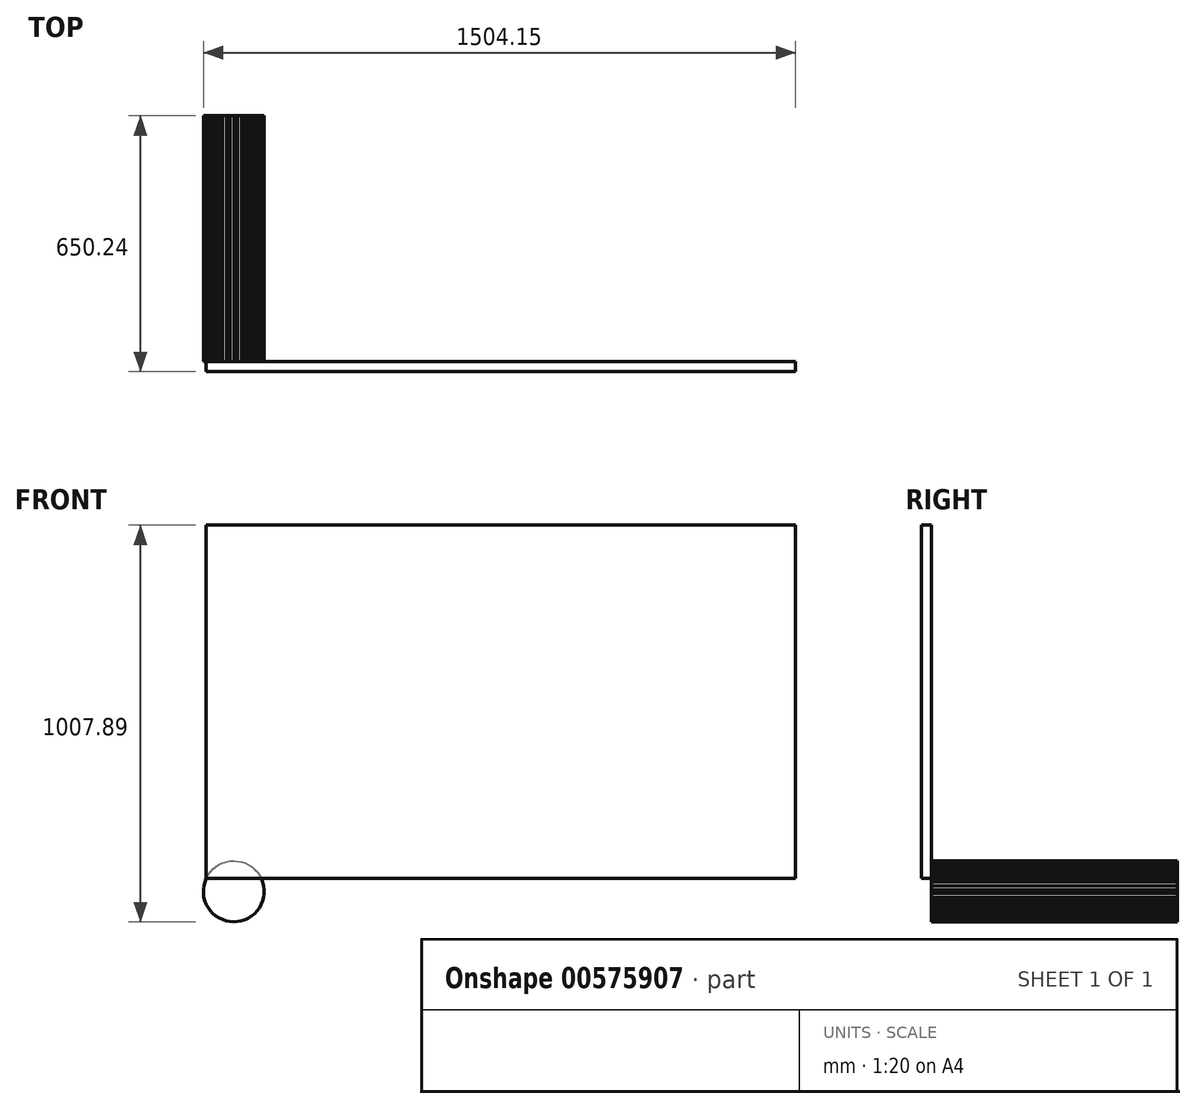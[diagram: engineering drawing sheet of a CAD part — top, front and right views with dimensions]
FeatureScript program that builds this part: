
annotation { "Feature Type Name" : "Feature", "Feature Type Description" : "" }
export const myFeature = defineFeature(function(context is Context, id is Id, definition is map)
    precondition{}
    {
        {
            var Q0;
            Q0=qCreatedBy(makeId("Front.planeOp"),FACE);
            var sketch = newSketch(context, id + "F0", { "sketchPlane" : qUnion([Q0])});
            skCircle(sketch, "E0.cCircle", {"center": v(-103.02, 63.84) * mm, "radius": 77.26 * mm, "construction": true});
            skLineSegment(sketch, "E0.0", {"start": v(-33.2, 30.4) * mm, "end": v(-37.94, 21.92) * mm});
            skLineSegment(sketch, "E0.1", {"start": v(-37.94, 21.92) * mm, "end": v(-43.7, 14.1) * mm});
            skLineSegment(sketch, "E0.2", {"start": v(-43.7, 14.1) * mm, "end": v(-50.4, 7.05) * mm});
            skLineSegment(sketch, "E0.3", {"start": v(-50.4, 7.05) * mm, "end": v(-57.94, 0.9) * mm});
            skLineSegment(sketch, "E0.4", {"start": v(-57.94, 0.9) * mm, "end": v(-66.18, -4.25) * mm});
            skLineSegment(sketch, "E0.5", {"start": v(-66.18, -4.25) * mm, "end": v(-75, -8.33) * mm});
            skLineSegment(sketch, "E0.6", {"start": v(-75, -8.33) * mm, "end": v(-84.27, -11.27) * mm});
            skLineSegment(sketch, "E0.7", {"start": v(-84.27, -11.27) * mm, "end": v(-93.84, -13.03) * mm});
            skLineSegment(sketch, "E0.8", {"start": v(-93.84, -13.03) * mm, "end": v(-103.54, -13.57) * mm});
            skLineSegment(sketch, "E0.9", {"start": v(-103.54, -13.57) * mm, "end": v(-113.24, -12.9) * mm});
            skLineSegment(sketch, "E0.10", {"start": v(-113.24, -12.9) * mm, "end": v(-122.78, -11) * mm});
            skLineSegment(sketch, "E0.11", {"start": v(-122.78, -11) * mm, "end": v(-132, -7.94) * mm});
            skLineSegment(sketch, "E0.12", {"start": v(-132, -7.94) * mm, "end": v(-140.77, -3.75) * mm});
            skLineSegment(sketch, "E0.13", {"start": v(-140.77, -3.75) * mm, "end": v(-148.94, 1.52) * mm});
            skLineSegment(sketch, "E0.14", {"start": v(-148.94, 1.52) * mm, "end": v(-156.39, 7.77) * mm});
            skLineSegment(sketch, "E0.15", {"start": v(-156.39, 7.77) * mm, "end": v(-163, 14.9) * mm});
            skLineSegment(sketch, "E0.16", {"start": v(-163, 14.9) * mm, "end": v(-168.66, 22.8) * mm});
            skLineSegment(sketch, "E0.17", {"start": v(-168.66, 22.8) * mm, "end": v(-173.28, 31.35) * mm});
            skLineSegment(sketch, "E0.18", {"start": v(-173.28, 31.35) * mm, "end": v(-176.8, 40.41) * mm});
            skLineSegment(sketch, "E0.19", {"start": v(-176.8, 40.41) * mm, "end": v(-179.15, 49.85) * mm});
            skLineSegment(sketch, "E0.20", {"start": v(-179.15, 49.85) * mm, "end": v(-180.3, 59.5) * mm});
            skLineSegment(sketch, "E0.21", {"start": v(-180.3, 59.5) * mm, "end": v(-180.24, 69.22) * mm});
            skLineSegment(sketch, "E0.22", {"start": v(-180.24, 69.22) * mm, "end": v(-178.96, 78.85) * mm});
            skLineSegment(sketch, "E0.23", {"start": v(-178.96, 78.85) * mm, "end": v(-176.47, 88.25) * mm});
            skLineSegment(sketch, "E0.24", {"start": v(-176.47, 88.25) * mm, "end": v(-172.84, 97.27) * mm});
            skLineSegment(sketch, "E0.25", {"start": v(-172.84, 97.27) * mm, "end": v(-168.1, 105.76) * mm});
            skLineSegment(sketch, "E0.26", {"start": v(-168.1, 105.76) * mm, "end": v(-162.33, 113.58) * mm});
            skLineSegment(sketch, "E0.27", {"start": v(-162.33, 113.58) * mm, "end": v(-155.63, 120.62) * mm});
            skLineSegment(sketch, "E0.28", {"start": v(-155.63, 120.62) * mm, "end": v(-148.1, 126.77) * mm});
            skLineSegment(sketch, "E0.29", {"start": v(-148.1, 126.77) * mm, "end": v(-139.85, 131.92) * mm});
            skLineSegment(sketch, "E0.30", {"start": v(-139.85, 131.92) * mm, "end": v(-131.03, 136) * mm});
            skLineSegment(sketch, "E0.31", {"start": v(-131.03, 136) * mm, "end": v(-121.76, 138.94) * mm});
            skLineSegment(sketch, "E0.32", {"start": v(-121.76, 138.94) * mm, "end": v(-112.2, 140.7) * mm});
            skLineSegment(sketch, "E0.33", {"start": v(-112.2, 140.7) * mm, "end": v(-102.5, 141.24) * mm});
            skLineSegment(sketch, "E0.34", {"start": v(-102.5, 141.24) * mm, "end": v(-92.8, 140.57) * mm});
            skLineSegment(sketch, "E0.35", {"start": v(-92.8, 140.57) * mm, "end": v(-83.26, 138.68) * mm});
            skLineSegment(sketch, "E0.36", {"start": v(-83.26, 138.68) * mm, "end": v(-74.03, 135.62) * mm});
            skLineSegment(sketch, "E0.37", {"start": v(-74.03, 135.62) * mm, "end": v(-65.27, 131.42) * mm});
            skLineSegment(sketch, "E0.38", {"start": v(-65.27, 131.42) * mm, "end": v(-57.1, 126.15) * mm});
            skLineSegment(sketch, "E0.39", {"start": v(-57.1, 126.15) * mm, "end": v(-49.65, 119.9) * mm});
            skLineSegment(sketch, "E0.40", {"start": v(-49.65, 119.9) * mm, "end": v(-43.04, 112.77) * mm});
            skLineSegment(sketch, "E0.41", {"start": v(-43.04, 112.77) * mm, "end": v(-37.38, 104.87) * mm});
            skLineSegment(sketch, "E0.42", {"start": v(-37.38, 104.87) * mm, "end": v(-32.75, 96.32) * mm});
            skLineSegment(sketch, "E0.43", {"start": v(-32.75, 96.32) * mm, "end": v(-29.24, 87.26) * mm});
            skLineSegment(sketch, "E0.44", {"start": v(-29.24, 87.26) * mm, "end": v(-26.88, 77.83) * mm});
            skLineSegment(sketch, "E0.45", {"start": v(-26.88, 77.83) * mm, "end": v(-25.73, 68.17) * mm});
            skLineSegment(sketch, "E0.46", {"start": v(-25.73, 68.17) * mm, "end": v(-25.8, 58.45) * mm});
            skLineSegment(sketch, "E0.47", {"start": v(-25.8, 58.45) * mm, "end": v(-27.08, 48.82) * mm});
            skLineSegment(sketch, "E0.48", {"start": v(-27.08, 48.82) * mm, "end": v(-29.56, 39.42) * mm});
            skLineSegment(sketch, "E0.49", {"start": v(-29.56, 39.42) * mm, "end": v(-33.2, 30.4) * mm});
            skPoint(sketch, "E0.0.midPoint", {"position": v(-35.57, 26.16) * mm});
            skSolve(sketch);
        }
        {
            var Q0;
            Q0 = qSketchRegion(id + "F0", true);
            extrude(context, id + "F1", {"entities" : qUnion([Q0]), "depth" : 599.44 * mm, "offsetDistance" : 25.4 * mm});
        }
        {
            var Q0;
            Q0=makeQuery(id+"F1.opExtrude","CAP_FACE",FACE,{"disambiguationData":[OSD([sQuery(id+"F0.wireOp",EDGE,"E0.0"),sQuery(id+"F0.wireOp",EDGE,"E0.1"),sQuery(id+"F0.wireOp",EDGE,"E0.2"),sQuery(id+"F0.wireOp",EDGE,"E0.3"),sQuery(id+"F0.wireOp",EDGE,"E0.4"),sQuery(id+"F0.wireOp",EDGE,"E0.5"),sQuery(id+"F0.wireOp",EDGE,"E0.6"),sQuery(id+"F0.wireOp",EDGE,"E0.7"),sQuery(id+"F0.wireOp",EDGE,"E0.8"),sQuery(id+"F0.wireOp",EDGE,"E0.9"),sQuery(id+"F0.wireOp",EDGE,"E0.10"),sQuery(id+"F0.wireOp",EDGE,"E0.11"),sQuery(id+"F0.wireOp",EDGE,"E0.12"),sQuery(id+"F0.wireOp",EDGE,"E0.13"),sQuery(id+"F0.wireOp",EDGE,"E0.14"),sQuery(id+"F0.wireOp",EDGE,"E0.15"),sQuery(id+"F0.wireOp",EDGE,"E0.16"),sQuery(id+"F0.wireOp",EDGE,"E0.17"),sQuery(id+"F0.wireOp",EDGE,"E0.18"),sQuery(id+"F0.wireOp",EDGE,"E0.19"),sQuery(id+"F0.wireOp",EDGE,"E0.20"),sQuery(id+"F0.wireOp",EDGE,"E0.21"),sQuery(id+"F0.wireOp",EDGE,"E0.22"),sQuery(id+"F0.wireOp",EDGE,"E0.23"),sQuery(id+"F0.wireOp",EDGE,"E0.24"),sQuery(id+"F0.wireOp",EDGE,"E0.25"),sQuery(id+"F0.wireOp",EDGE,"E0.26"),sQuery(id+"F0.wireOp",EDGE,"E0.27"),sQuery(id+"F0.wireOp",EDGE,"E0.28"),sQuery(id+"F0.wireOp",EDGE,"E0.29"),sQuery(id+"F0.wireOp",EDGE,"E0.30"),sQuery(id+"F0.wireOp",EDGE,"E0.31"),sQuery(id+"F0.wireOp",EDGE,"E0.32"),sQuery(id+"F0.wireOp",EDGE,"E0.33"),sQuery(id+"F0.wireOp",EDGE,"E0.34"),sQuery(id+"F0.wireOp",EDGE,"E0.35"),sQuery(id+"F0.wireOp",EDGE,"E0.36"),sQuery(id+"F0.wireOp",EDGE,"E0.37"),sQuery(id+"F0.wireOp",EDGE,"E0.38"),sQuery(id+"F0.wireOp",EDGE,"E0.39"),sQuery(id+"F0.wireOp",EDGE,"E0.40"),sQuery(id+"F0.wireOp",EDGE,"E0.41"),sQuery(id+"F0.wireOp",EDGE,"E0.42"),sQuery(id+"F0.wireOp",EDGE,"E0.43"),sQuery(id+"F0.wireOp",EDGE,"E0.44"),sQuery(id+"F0.wireOp",EDGE,"E0.45"),sQuery(id+"F0.wireOp",EDGE,"E0.46"),sQuery(id+"F0.wireOp",EDGE,"E0.47"),sQuery(id+"F0.wireOp",EDGE,"E0.48"),sQuery(id+"F0.wireOp",EDGE,"E0.49")])],"isStart":false});
            extrude(context, id + "F2", {"entities" : qUnion([Q0]), "operationType" : NewBodyOperationType.ADD, "depth" : 25.4 * mm, "offsetDistance" : 25.4 * mm});
        }
        {
            var Q0;
            Q0=makeQuery(id+"F2.opExtrude","CAP_FACE",FACE,{"disambiguationData":[OSD([sQuery(id+"F0.wireOp",EDGE,"E0.0"),sQuery(id+"F0.wireOp",EDGE,"E0.1"),sQuery(id+"F0.wireOp",EDGE,"E0.2"),sQuery(id+"F0.wireOp",EDGE,"E0.3"),sQuery(id+"F0.wireOp",EDGE,"E0.4"),sQuery(id+"F0.wireOp",EDGE,"E0.5"),sQuery(id+"F0.wireOp",EDGE,"E0.6"),sQuery(id+"F0.wireOp",EDGE,"E0.7"),sQuery(id+"F0.wireOp",EDGE,"E0.8"),sQuery(id+"F0.wireOp",EDGE,"E0.9"),sQuery(id+"F0.wireOp",EDGE,"E0.10"),sQuery(id+"F0.wireOp",EDGE,"E0.11"),sQuery(id+"F0.wireOp",EDGE,"E0.12"),sQuery(id+"F0.wireOp",EDGE,"E0.13"),sQuery(id+"F0.wireOp",EDGE,"E0.14"),sQuery(id+"F0.wireOp",EDGE,"E0.15"),sQuery(id+"F0.wireOp",EDGE,"E0.16"),sQuery(id+"F0.wireOp",EDGE,"E0.17"),sQuery(id+"F0.wireOp",EDGE,"E0.18"),sQuery(id+"F0.wireOp",EDGE,"E0.19"),sQuery(id+"F0.wireOp",EDGE,"E0.20"),sQuery(id+"F0.wireOp",EDGE,"E0.21"),sQuery(id+"F0.wireOp",EDGE,"E0.22"),sQuery(id+"F0.wireOp",EDGE,"E0.23"),sQuery(id+"F0.wireOp",EDGE,"E0.24"),sQuery(id+"F0.wireOp",EDGE,"E0.25"),sQuery(id+"F0.wireOp",EDGE,"E0.26"),sQuery(id+"F0.wireOp",EDGE,"E0.27"),sQuery(id+"F0.wireOp",EDGE,"E0.28"),sQuery(id+"F0.wireOp",EDGE,"E0.29"),sQuery(id+"F0.wireOp",EDGE,"E0.30"),sQuery(id+"F0.wireOp",EDGE,"E0.31"),sQuery(id+"F0.wireOp",EDGE,"E0.32"),sQuery(id+"F0.wireOp",EDGE,"E0.33"),sQuery(id+"F0.wireOp",EDGE,"E0.34"),sQuery(id+"F0.wireOp",EDGE,"E0.35"),sQuery(id+"F0.wireOp",EDGE,"E0.36"),sQuery(id+"F0.wireOp",EDGE,"E0.37"),sQuery(id+"F0.wireOp",EDGE,"E0.38"),sQuery(id+"F0.wireOp",EDGE,"E0.39"),sQuery(id+"F0.wireOp",EDGE,"E0.40"),sQuery(id+"F0.wireOp",EDGE,"E0.41"),sQuery(id+"F0.wireOp",EDGE,"E0.42"),sQuery(id+"F0.wireOp",EDGE,"E0.43"),sQuery(id+"F0.wireOp",EDGE,"E0.44"),sQuery(id+"F0.wireOp",EDGE,"E0.45"),sQuery(id+"F0.wireOp",EDGE,"E0.46"),sQuery(id+"F0.wireOp",EDGE,"E0.47"),sQuery(id+"F0.wireOp",EDGE,"E0.48"),sQuery(id+"F0.wireOp",EDGE,"E0.49")])],"isStart":false});
            var sketch = newSketch(context, id + "F3", { "sketchPlane" : qUnion([Q0])});
            skLineSegment(sketch, "E1.bottom", {"start": v(-172.84, 97.27) * mm, "end": v(1323.84, 97.27) * mm});
            skLineSegment(sketch, "E1.top", {"start": v(-172.84, 994.32) * mm, "end": v(1323.84, 994.32) * mm});
            skLineSegment(sketch, "E1.left", {"start": v(-172.84, 97.27) * mm, "end": v(-172.84, 994.32) * mm});
            skLineSegment(sketch, "E1.right", {"start": v(1323.84, 97.27) * mm, "end": v(1323.84, 994.32) * mm});
            skSolve(sketch);
        }
        {
            var Q0;
            Q0 = qSketchRegion(id + "F3", true);
            extrude(context, id + "F4", {"entities" : qUnion([Q0]), "operationType" : NewBodyOperationType.ADD, "depth" : 25.4 * mm, "offsetDistance" : 25.4 * mm});
        }
    });
